# Revit family: Indoor_Pendant Lamp_Santa&Cole_Globo Cesta
name_source: partatom
category: Luminarias
revit_build: Autodesk Revit 2018 (Build: 20190510_1515(x64)
units: mm (PartAtom-declared; Revit-internal decimal feet)

## family parameters
Anfitrión = Cara
Compartido = No
Corte con vacíos al cargar = No
Cota de conector redondo = Diámetro de uso
Origen de luz = Sí
Punto de cálculo de habitación = No
Tipo de pieza = Normal

## types (2) — shared parameters
Assembly Instructions - CE = https://www.santacole.com
Cambio de temperatura de color de luz atenuada = <Ninguno>
Code = CES15
Elevación por defecto = 1219 mm
Energy Label = https://www.santacole.com
Fabricante = Santa & Cole
Filtro de color = 16777215
Manufacturer website = http://www.santacole.com
Modelo = Globo Cesta
Tamaño de símbolo de origen de luz = 50 mm  [stored 0.164042 ft]
Technical Information = https://www.santacole.com
URL = https://www.santacole.com
Voltaje (90-305 V) = 220 V

## per-type parameters (varying)
| type | Carga aparente | Ligth Source Elevation | Load | Longitud de línea de emisión | Visibility_Globo Cesta | Visibility_Globo Cestita |
| Globo Cesta | 12 W | 1200 mm | 12 W | 50 mm  [stored 0.164042 ft] | Sí | No |
| Globo Cestita | 5 W | 740 mm  [stored 2.42782 ft] | 5 W | 610 mm | No | Sí |

note: [stored X ft] marks values corroborated as IEEE doubles in the binary element streams (Revit-internal decimal feet)

## geometry (parser evidence)
native form markers: Sweep x2
no freeform markers — native parametric forms only
